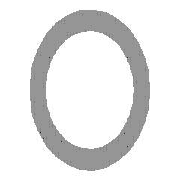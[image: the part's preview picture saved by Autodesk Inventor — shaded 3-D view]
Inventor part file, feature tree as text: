
AUTODESK INVENTOR PART (.ipt)
format: ipt  version: 2021 (Build 250183000, 183)  size: 382,976 bytes
history: native  units: mm (DEFAULTED — no unit token found)
features: other x5, plane x2, sketch x2, sweep x1
ambient origin geometry x8: Origin, YZ Plane, XZ Plane, XY Plane, X Axis, Y Axis, Z Axis, Center Point
bodies: Solid1 (feature_tree)
feature tree (10):
  parser-record x1  (decoder bookkeeping rows leaked as tree rows — omitted from the tree; the rows remain in map.json)
  other  "Driven Length"
  other  "Plano inicial"
  other  "Plano final"
  other  "Trayectoria de barrido"
  plane  "Plano de trabajo de orientación"
  sweep  "Cuerpo"
  sketch  "Sketch3"  dims[d0=26.67mm d1=3.9116mm]
  plane  "Work Plane3"
  sketch  "Sketch4"  dims[d4=-0.0mm d5=1165.819732mm d6=90.0deg d7=1165.819732mm d8=0.0mm d9=0.0mm]
